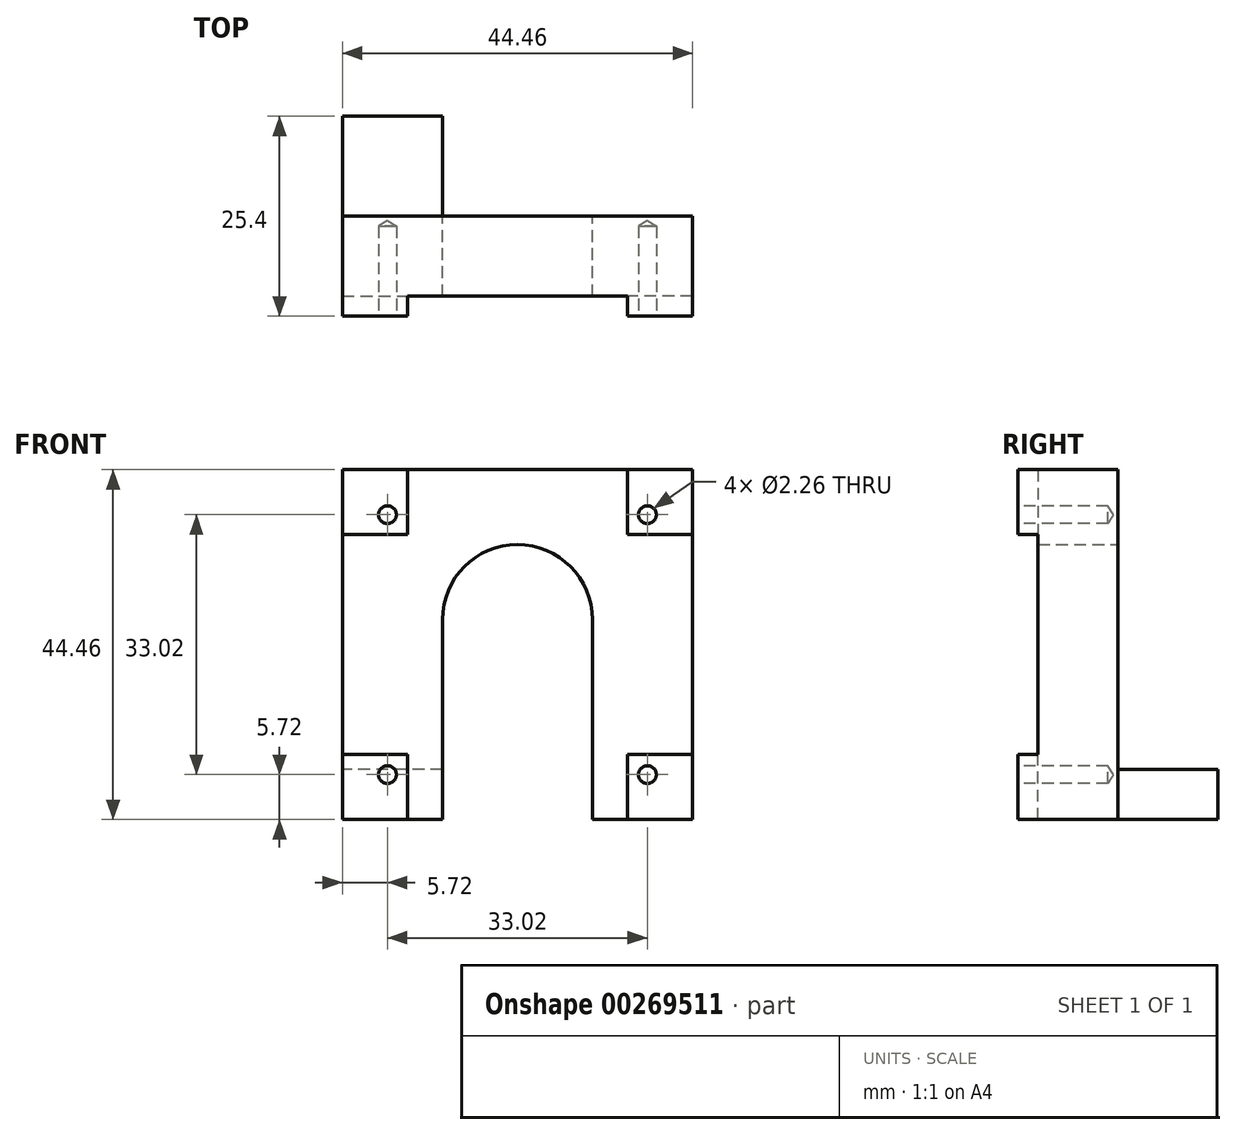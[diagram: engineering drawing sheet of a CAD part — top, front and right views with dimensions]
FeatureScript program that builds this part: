
annotation { "Feature Type Name" : "Feature", "Feature Type Description" : "" }
export const myFeature = defineFeature(function(context is Context, id is Id, definition is map)
    precondition{}
    {
        {
            var Q0;
            Q0=qCreatedBy(makeId("Front.planeOp"),FACE);
            var sketch = newSketch(context, id + "F0", { "sketchPlane" : qUnion([Q0])});
            skLineSegment(sketch, "E0.bottom", {"start": v(22.23, -22.22) * mm, "end": v(-22.23, -22.22) * mm});
            skLineSegment(sketch, "E0.top", {"start": v(22.22, 22.23) * mm, "end": v(-22.23, 22.23) * mm});
            skLineSegment(sketch, "E0.left", {"start": v(22.23, -22.22) * mm, "end": v(22.22, 22.23) * mm});
            skLineSegment(sketch, "E0.right", {"start": v(-22.23, -22.22) * mm, "end": v(-22.23, 22.23) * mm});
            skPoint(sketch, "E0.middle", {"position": v(0, 0) * mm});
            skSolve(sketch);
        }
        {
            var Q0;
            Q0=qSketchRegion(id+"F0",true);
            extrude(context, id + "F1", {"entities" : qUnion([Q0]), "depth" : 12.7 * mm});
        }
        {
            var Q0;
            Q0=makeQuery(id+"F1.opExtrude","SWEPT_FACE",FACE,{"disambiguationData":[OSD([sQuery(id+"F0.wireOp",EDGE,"E0.right")])]});
            var sketch = newSketch(context, id + "F2", { "sketchPlane" : qUnion([Q0])});
            skLineSegment(sketch, "E1.bottom", {"start": v(0, -22.22) * mm, "end": v(-12.7, -22.22) * mm});
            skLineSegment(sketch, "E1.top", {"start": v(0, -15.87) * mm, "end": v(-12.7, -15.87) * mm});
            skLineSegment(sketch, "E1.left", {"start": v(0, -22.22) * mm, "end": v(0, -15.87) * mm});
            skLineSegment(sketch, "E1.right", {"start": v(-12.7, -22.22) * mm, "end": v(-12.7, -15.88) * mm});
            skSolve(sketch);
        }
        {
            var Q0;
            Q0=qSketchRegion(id+"F2",true);
            extrude(context, id + "F3", {"entities" : qUnion([Q0]), "operationType" : NewBodyOperationType.ADD, "oppositeDirection" : true, "depth" : 12.7 * mm});
        }
        {
            var Q0;
            Q0=makeQuery(id+"F1.opExtrude","CAP_FACE",FACE,{"disambiguationData":[OSD([sQuery(id+"F0.wireOp",EDGE,"E0.bottom"),sQuery(id+"F0.wireOp",EDGE,"E0.top"),sQuery(id+"F0.wireOp",EDGE,"E0.left"),sQuery(id+"F0.wireOp",EDGE,"E0.right")])],"isStart":false});
            var sketch = newSketch(context, id + "F4", { "sketchPlane" : qUnion([Q0])});
            skLineSegment(sketch, "E2.bottom", {"start": v(16.5, 16.51) * mm, "end": v(-16.51, 16.51) * mm, "construction": true});
            skLineSegment(sketch, "E2.top", {"start": v(16.5, -16.51) * mm, "end": v(-16.51, -16.51) * mm, "construction": true});
            skLineSegment(sketch, "E2.left", {"start": v(16.5, 16.51) * mm, "end": v(16.5, -16.51) * mm, "construction": true});
            skLineSegment(sketch, "E2.right", {"start": v(-16.51, 16.51) * mm, "end": v(-16.51, -16.51) * mm, "construction": true});
            skPoint(sketch, "E2.middle", {"position": v(0, 0) * mm});
            skLineSegment(sketch, "E3.bottom", {"start": v(-22.23, 22.23) * mm, "end": v(-13.97, 22.23) * mm, "construction": true});
            skLineSegment(sketch, "E3.top", {"start": v(-22.23, 13.97) * mm, "end": v(-13.97, 13.97) * mm});
            skLineSegment(sketch, "E3.left", {"start": v(-22.23, 22.23) * mm, "end": v(-22.23, 13.97) * mm, "construction": true});
            skLineSegment(sketch, "E3.right", {"start": v(-13.97, 22.23) * mm, "end": v(-13.97, 13.97) * mm});
            skLineSegment(sketch, "E4", {"start": v(0, 22.23) * mm, "end": v(0, -22.23) * mm, "construction": true});
            skLineSegment(sketch, "E5", {"start": v(-22.23, 0) * mm, "end": v(22.23, 0) * mm, "construction": true});
            skPoint(sketch, "E5.startSnap0", {"position": v(-16.51, 0) * mm});
            skPoint(sketch, "E5.endSnap0", {"position": v(16.51, 0) * mm});
            skLineSegment(sketch, "E6", {"start": v(-13.97, 22.23) * mm, "end": v(0, 22.23) * mm});
            skLineSegment(sketch, "E7", {"start": v(-22.23, 13.97) * mm, "end": v(-22.23, 0) * mm});
            skLineSegment(sketch, "E8.MirrorCS", {"start": v(13.97, 22.23) * mm, "end": v(13.97, 13.97) * mm});
            skLineSegment(sketch, "E9.MirrorCS", {"start": v(22.23, 13.97) * mm, "end": v(13.97, 13.97) * mm});
            skLineSegment(sketch, "E10.MirrorCS", {"start": v(22.23, 13.97) * mm, "end": v(22.23, 0) * mm});
            skLineSegment(sketch, "E11.MirrorCS", {"start": v(13.97, 22.22) * mm, "end": v(0, 22.22) * mm});
            skLineSegment(sketch, "E12.MirrorCS", {"start": v(-22.23, -13.97) * mm, "end": v(-22.23, 0) * mm});
            skLineSegment(sketch, "E13.MirrorCS", {"start": v(-22.23, -13.97) * mm, "end": v(-13.97, -13.97) * mm});
            skLineSegment(sketch, "E14.MirrorCS", {"start": v(-13.97, -22.23) * mm, "end": v(-13.97, -13.97) * mm});
            skLineSegment(sketch, "E15.MirrorCS", {"start": v(-13.97, -22.23) * mm, "end": v(0, -22.23) * mm});
            skLineSegment(sketch, "E16.MirrorCS", {"start": v(13.97, -22.22) * mm, "end": v(0, -22.22) * mm});
            skLineSegment(sketch, "E17.MirrorCS", {"start": v(13.97, -22.23) * mm, "end": v(13.97, -13.97) * mm});
            skLineSegment(sketch, "E18.MirrorCS", {"start": v(22.23, -13.97) * mm, "end": v(13.97, -13.97) * mm});
            skLineSegment(sketch, "E19", {"start": v(22.23, 0) * mm, "end": v(22.23, -13.97) * mm});
            skSolve(sketch);
        }
        {
            var Q0;
            Q0=qSketchRegion(id+"F4",true);
            extrude(context, id + "F5", {"entities" : qUnion([Q0]), "operationType" : NewBodyOperationType.REMOVE, "oppositeDirection" : true, "depth" : 2.54 * mm});
        }
        {
            var Q0;
            Q0=sQuery(id+"F4.wireOp",VERTEX,"E2.right.start");
            var Q1;
            Q1=sQuery(id+"F4.wireOp",VERTEX,"E2.left.start");
            var Q2;
            Q2=sQuery(id+"F4.wireOp",VERTEX,"E2.left.end");
            var Q3;
            Q3=sQuery(id+"F4.wireOp",VERTEX,"E2.right.end");
            var Q4;
            Q4=makeQuery(id+"F1.opExtrude","SWEPT_BODY",BODY,{"disambiguationData":[OSD([sQuery(id+"F0.wireOp",EDGE,"E0.bottom"),sQuery(id+"F0.wireOp",EDGE,"E0.top"),sQuery(id+"F0.wireOp",EDGE,"E0.left"),sQuery(id+"F0.wireOp",EDGE,"E0.right")])]});
            hole(context, id + "F6", {"style" : HoleStyle.SIMPLE, "endStyle" : HoleEndStyle.BLIND, "standardTappedOrClearance" : lookupTablePath({ "standard" : "ANSI", "engagement" : "75%", "pitch" : "40 tpi", "size" : "#4", "type" : "Tapped" }), "standardBlindInLast" : lookupTablePath({ "standard" : "ANSI", "engagement" : "75%", "pitch" : "40 tpi", "size" : "#4", "type" : "Tapped" }), "holeDiameter" : 2.26 * mm, "showTappedDepth" : true, "holeDepth" : 11.43 * mm, "tappedDepth" : 9.52 * mm, "tapClearance" : 3, "locations" : qUnion([Q0, Q1, Q2, Q3]), "scope" : qUnion([Q4]), "majorDiameter" : 2.84 * mm});
        }
        {
            var Q0;
            {var subQ0=sQuery(id+"F2.wireOp",EDGE,"E1.bottom");Q0=makeQuery(id+"FwmCJXWThpcOfOr_1.1.F3.boolean.opBoolean","MERGE",FACE,{"derivedFrom":[makeQuery(id+"F3.boolean.opBoolean","MERGE",FACE,{"derivedFrom":[makeQuery(id+"F1.opExtrude","SWEPT_FACE",FACE,{"disambiguationData":[OSD([sQuery(id+"F0.wireOp",EDGE,"E0.bottom")])]}),makeQuery(id+"F3.opExtrude","SWEPT_FACE",FACE,{"disambiguationData":[OSD([subQ0])]})]}),makeQuery(id+"FwmCJXWThpcOfOr_1.1.F3.opExtrude","SWEPT_FACE",FACE,{"disambiguationData":[OSD([subQ0])]})]});}
            var sketch = newSketch(context, id + "F7", { "sketchPlane" : qUnion([Q0])});
            skLineSegment(sketch, "E20.bottom", {"start": v(15.87, -3.18) * mm, "end": v(15.87, -3.18) * mm});
            skLineSegment(sketch, "E20.top", {"start": v(15.87, -9.53) * mm, "end": v(15.87, -9.53) * mm});
            skLineSegment(sketch, "E20.left", {"start": v(18.12, -5.42) * mm, "end": v(18.12, -7.28) * mm});
            skLineSegment(sketch, "E20.right", {"start": v(13.63, -5.42) * mm, "end": v(13.63, -7.28) * mm});
            skPoint(sketch, "E20.middle", {"position": v(15.87, -6.35) * mm});
            skPoint(sketch, "E21.visualSharp", {"position": v(13.63, -3.18) * mm});
            skArc(sketch, "E21.filletArc", {"start": v(15.87, -3.18) * mm, "mid": v(14.29, -3.83) * mm, "end": v(13.63, -5.42) * mm});
            skPoint(sketch, "E22.visualSharp", {"position": v(18.12, -3.18) * mm});
            skArc(sketch, "E22.filletArc", {"start": v(18.12, -5.42) * mm, "mid": v(17.46, -3.83) * mm, "end": v(15.87, -3.18) * mm});
            skPoint(sketch, "E23.visualSharp", {"position": v(18.12, -9.53) * mm});
            skArc(sketch, "E23.filletArc", {"start": v(15.87, -9.53) * mm, "mid": v(17.46, -8.87) * mm, "end": v(18.12, -7.28) * mm});
            skPoint(sketch, "E24.visualSharp", {"position": v(13.63, -9.53) * mm});
            skArc(sketch, "E24.filletArc", {"start": v(13.63, -7.28) * mm, "mid": v(14.29, -8.87) * mm, "end": v(15.87, -9.53) * mm});
            skLineSegment(sketch, "E25", {"start": v(15.87, -12.7) * mm, "end": v(15.87, 0) * mm, "construction": true});
            skSolve(sketch);
        }
        {
            var Q0;
            Q0=makeQuery(id+"F1.opExtrude","CAP_FACE",FACE,{"disambiguationData":[OSD([sQuery(id+"F0.wireOp",EDGE,"E0.bottom"),sQuery(id+"F0.wireOp",EDGE,"E0.top"),sQuery(id+"F0.wireOp",EDGE,"E0.left"),sQuery(id+"F0.wireOp",EDGE,"E0.right")])],"isStart":true});
            var sketch = newSketch(context, id + "F8", { "sketchPlane" : qUnion([Q0])});
            skLineSegment(sketch, "E26.bottom", {"start": v(-9.53, -22.22) * mm, "end": v(9.52, -22.22) * mm});
            skLineSegment(sketch, "E26.top", {"start": v(-9.53, 3.18) * mm, "end": v(9.52, 3.18) * mm, "construction": true});
            skLineSegment(sketch, "E26.left", {"start": v(-9.53, -22.22) * mm, "end": v(-9.53, 3.18) * mm});
            skLineSegment(sketch, "E26.right", {"start": v(9.53, -22.22) * mm, "end": v(9.52, 3.18) * mm});
            skArc(sketch, "E27", {"start": v(9.52, 3.18) * mm, "mid": v(0, 12.7) * mm, "end": v(-9.53, 3.18) * mm});
            skSolve(sketch);
        }
        {
            var Q0;
            Q0=qSketchRegion(id+"F8",true);
            var Q1;
            Q1=sQuery(id+"F8.wireOp",EDGE,"E27");
            extrude(context, id + "F9", {"entities" : qUnion([Q0]), "operationType" : NewBodyOperationType.REMOVE, "surfaceEntities" : qUnion([Q1]), "endBound" : BoundingType.THROUGH_ALL, "oppositeDirection" : true, "depth" : 25.4 * mm});
        }
        {
            var Q0;
            Q0=sQuery(id+"F7.wireOp",VERTEX,"E20.middle");
            var Q1;
            Q1=makeQuery(id+"F1.opExtrude","SWEPT_BODY",BODY,{"disambiguationData":[OSD([sQuery(id+"F0.wireOp",EDGE,"E0.bottom"),sQuery(id+"F0.wireOp",EDGE,"E0.top"),sQuery(id+"F0.wireOp",EDGE,"E0.left"),sQuery(id+"F0.wireOp",EDGE,"E0.right")])]});
            hole(context, id + "F10", {"style" : HoleStyle.SIMPLE, "endStyle" : HoleEndStyle.THROUGH, "standardTappedOrClearance" : lookupTablePath({ "standard" : "ANSI", "fit" : "Normal (ASME)", "size" : "#8", "type" : "Clearance" }), "standardBlindInLast" : lookupTablePath({ "fit" : "Free", "standard" : "ANSI", "size" : "#8", "type" : "Clearance" }), "holeDiameter" : 4.5 * mm, "tappedDepth" : 9.52 * mm, "tapClearance" : 3, "locations" : qUnion([Q0]), "scope" : qUnion([Q1])});
        }
    });
